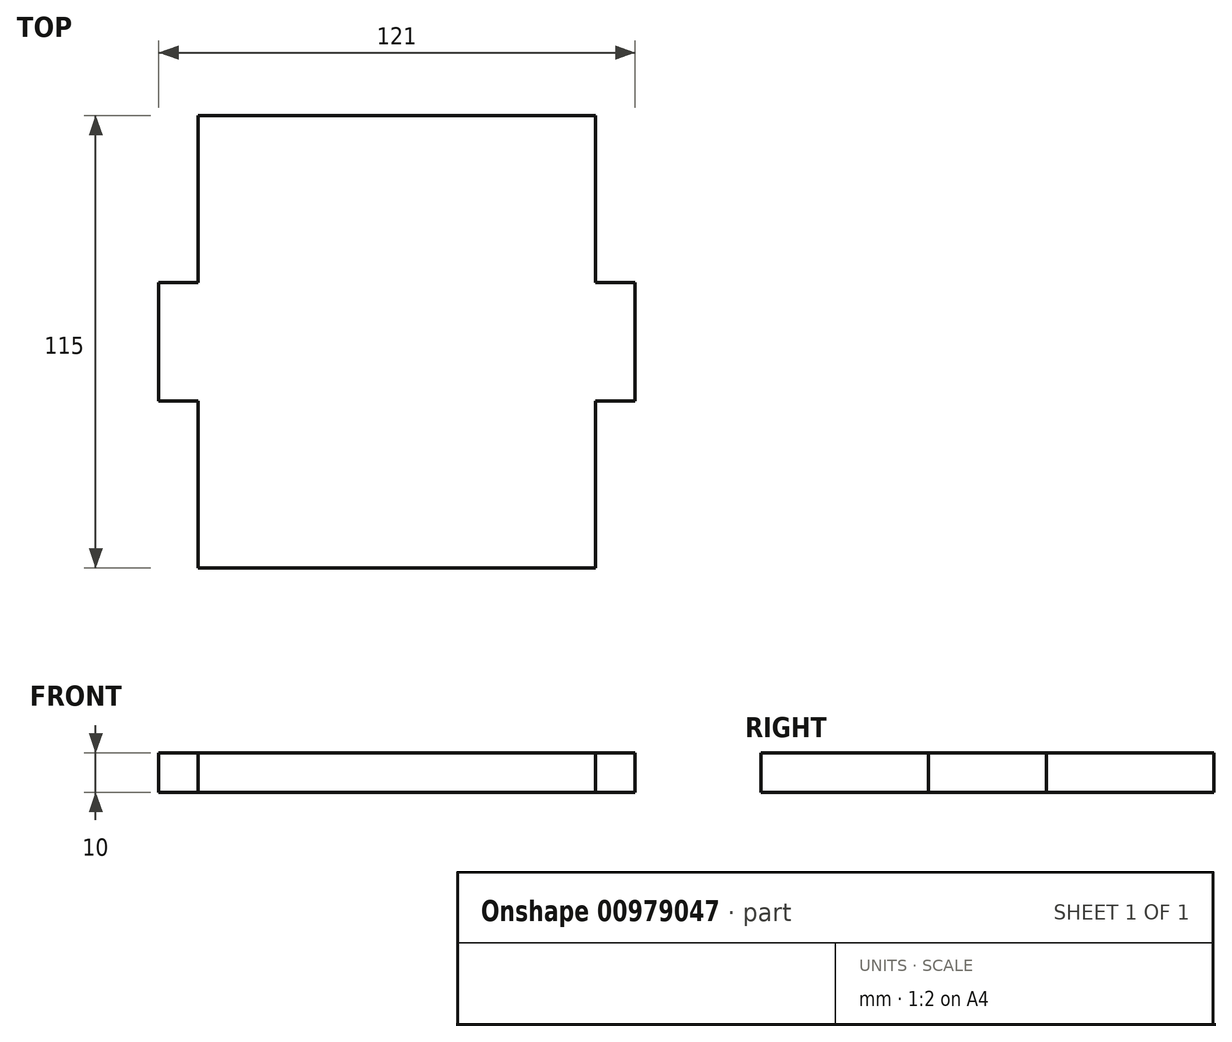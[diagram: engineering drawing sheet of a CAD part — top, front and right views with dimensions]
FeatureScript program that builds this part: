
annotation { "Feature Type Name" : "Feature", "Feature Type Description" : "" }
export const myFeature = defineFeature(function(context is Context, id is Id, definition is map)
    precondition{}
    {
        {
            var Q0;
            Q0=qCreatedBy(makeId("Top.planeOp"),FACE);
            var sketch = newSketch(context, id + "F0", { "sketchPlane" : qUnion([Q0])});
            skLineSegment(sketch, "E0.bottom", {"start": v(226.88, 59.81) * mm, "end": v(327.88, 59.81) * mm});
            skLineSegment(sketch, "E0.top", {"start": v(226.88, -55.19) * mm, "end": v(327.88, -55.19) * mm});
            skLineSegment(sketch, "E1", {"start": v(226.88, 59.81) * mm, "end": v(226.88, 17.31) * mm});
            skLineSegment(sketch, "E2", {"start": v(226.88, 17.31) * mm, "end": v(216.88, 17.31) * mm});
            skLineSegment(sketch, "E3", {"start": v(216.88, 17.31) * mm, "end": v(216.88, -12.69) * mm});
            skLineSegment(sketch, "E4", {"start": v(216.88, -12.69) * mm, "end": v(226.88, -12.69) * mm});
            skLineSegment(sketch, "E5", {"start": v(226.88, -12.69) * mm, "end": v(226.88, -55.19) * mm});
            skLineSegment(sketch, "E6", {"start": v(327.88, 59.81) * mm, "end": v(327.88, 17.31) * mm});
            skLineSegment(sketch, "E7", {"start": v(327.88, 17.31) * mm, "end": v(337.88, 17.31) * mm});
            skLineSegment(sketch, "E8", {"start": v(337.88, 17.31) * mm, "end": v(337.88, -12.69) * mm});
            skLineSegment(sketch, "E9", {"start": v(337.88, -12.69) * mm, "end": v(327.88, -12.69) * mm});
            skLineSegment(sketch, "E10", {"start": v(327.88, -12.69) * mm, "end": v(327.88, -55.19) * mm});
            skSolve(sketch);
        }
        {
            var Q0;
            Q0=makeQuery(id+"F0.imprint","IMPRINT",FACE,{"disambiguationData":[TD([[makeQuery(id+"F0.imprint","IMPRINT",EDGE,{"derivedFrom":sQuery(id+"F0.wireOp",EDGE,"E0.bottom")}),-1.0]])]});
            extrude(context, id + "F1", {"entities" : qUnion([Q0]), "depth" : 10 * mm, "offsetDistance" : 25 * mm});
        }
    });
